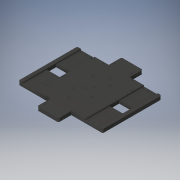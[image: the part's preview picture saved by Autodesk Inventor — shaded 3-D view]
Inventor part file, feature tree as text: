
AUTODESK INVENTOR PART (.ipt)
format: ipt  version: 2017 (Build 210142000, 142)  size: 487,424 bytes
history: native  units: in
note: dims shown in document units (in); Inventor stores cm internally (conversion verified against a paired STEP export)
features: extrude x10, sketch x10, projected_geometry x10, fillet x1
ambient origin geometry x8: Origin, YZ Plane, XZ Plane, XY Plane, X Axis, Y Axis, Z Axis, Center Point
bodies: Solid1 (feature_tree)
feature tree (31):
  extrude  "Extrusion1"  Depth=9.0in
  extrude  "Extrusion2"  Depth=1.118in
  extrude  "Extrusion3"  Depth=0.25in
  extrude  "Extrusion4"  TaperAngle=0.0deg  [1 undecoded]
  extrude  "Extrusion5"  Depth=0.375in
  extrude  "Extrusion7"  Depth=0.125in
  extrude  "ardMount"  Depth=0.125in TaperAngle=0.0deg
  extrude  "piMount"  Depth=0.125in TaperAngle=0.0deg
  extrude  "sabertoothMount"  Depth=3.0in
  extrude  "Extrusion11"  Depth=0.125in TaperAngle=0.0deg
  fillet  "Fillet1"  Radius=1.368in
  sketch  "Sketch1"  dims[d0=9.0in d1=9.0in]
  sketch  "Sketch2"  dims[d2=2.3622in d3=1.118in]
  projected_geometry  "Projected Loop1"
  sketch  "Sketch3"  dims[d4=0.375in d5=0.0in d6=0.25in]
  projected_geometry  "Projected Loop2"
  projected_geometry  "Projected Loop3"
  projected_geometry  "Projected Loop4"
  projected_geometry  "Projected Loop5"
  sketch  "Sketch4"  dims[d7=0.375in d8=0.0in]
  sketch  "Sketch5"  dims[d9=1.5in d10=0.375in]
  sketch  "Sketch7"  dims[d11=0.125in d12=0.5827in]
  projected_geometry  "Projected Loop7"
  sketch  "Sketch8"  dims[d13=0.125in d14=0.0312in d15=0.0in]
  projected_geometry  "Projected Loop8"
  sketch  "Sketch9"  dims[d16=0.125in d17=0.0in d18=0.125in d19=0.0in]
  projected_geometry  "Projected Loop9"
  sketch  "Sketch10"  dims[d20=1.5in d21=3.0in]
  projected_geometry  "Projected Loop10"
  sketch  "Sketch11"  dims[d22=0.125in d23=0.125in d24=0.0in d30=1.368in d31=1.0in d32=0.0in d33=0.209in d34=3.543in d35=0.63in d36=0.209in d37=0.571in d38=3.799in d39=0.125in d40=0.125in d41=0.125in d42=0.125in d43=1.0in d44=0.0in d45=0.184in d46=0.93in d47=3.21in d48=0.125in d49=0.125in d50=1.0in d51=0.0in d52=2.026in d53=2.859in d54=1.121in d55=4.275in d56=2.026in d57=2.859in d58=1.121in d59=4.275in d60=0.125in d61=0.125in d62=0.125in d63=0.125in d64=0.125in d65=0.125in d66=0.125in d67=0.125in d68=1.0in d69=0.0in d70=1.0in d71=1.0in d72=0.0in d73=0.125in]
  projected_geometry  "Projected Loop11"
note: 1 required parameter value undecoded (feature->parameter linkage not recoverable at this tier; creation-order binding heuristic only, values carry confidence <= 0.55)
